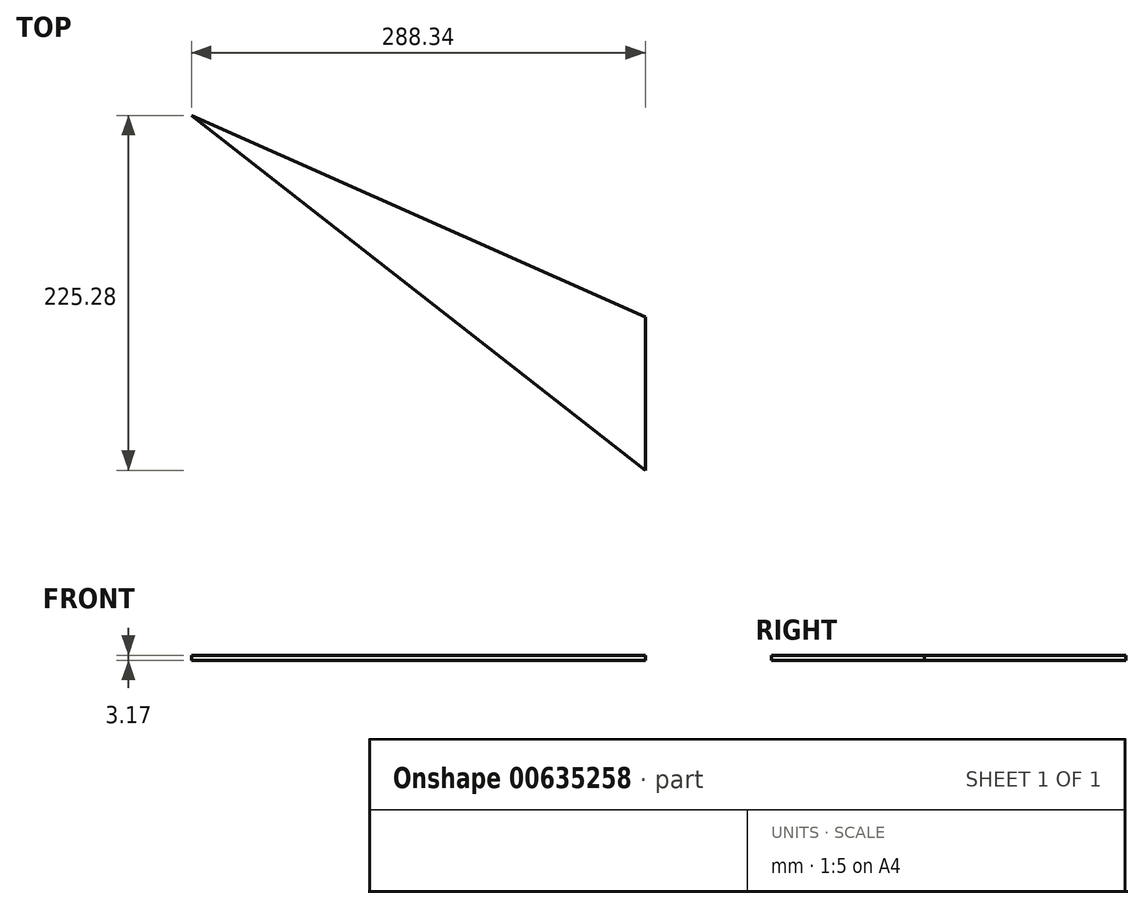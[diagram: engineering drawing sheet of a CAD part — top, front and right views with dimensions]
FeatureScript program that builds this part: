
annotation { "Feature Type Name" : "Feature", "Feature Type Description" : "" }
export const myFeature = defineFeature(function(context is Context, id is Id, definition is map)
    precondition{}
    {
        {
            var Q0;
            Q0=qCreatedBy(makeId("Top.planeOp"),FACE);
            var sketch = newSketch(context, id + "F0", { "sketchPlane" : qUnion([Q0])});
            skLineSegment(sketch, "E0", {"start": v(0, 0) * mm, "end": v(0, 97.26) * mm});
            skLineSegment(sketch, "E1", {"start": v(-288.34, 225.28) * mm, "end": v(0, 0) * mm});
            skLineSegment(sketch, "E2", {"start": v(-288.34, 225.28) * mm, "end": v(0, 97.26) * mm});
            skSolve(sketch);
        }
        {
            var Q0;
            Q0=makeQuery(id+"F0.imprint","IMPRINT",FACE,{"disambiguationData":[TD([[makeQuery(id+"F0.imprint","IMPRINT",EDGE,{"derivedFrom":sQuery(id+"F0.wireOp",EDGE,"E0")}),1.0]])]});
            extrude(context, id + "F1", {"entities" : qUnion([Q0]), "depth" : 3.17 * mm, "offsetDistance" : 25.4 * mm});
        }
    });
